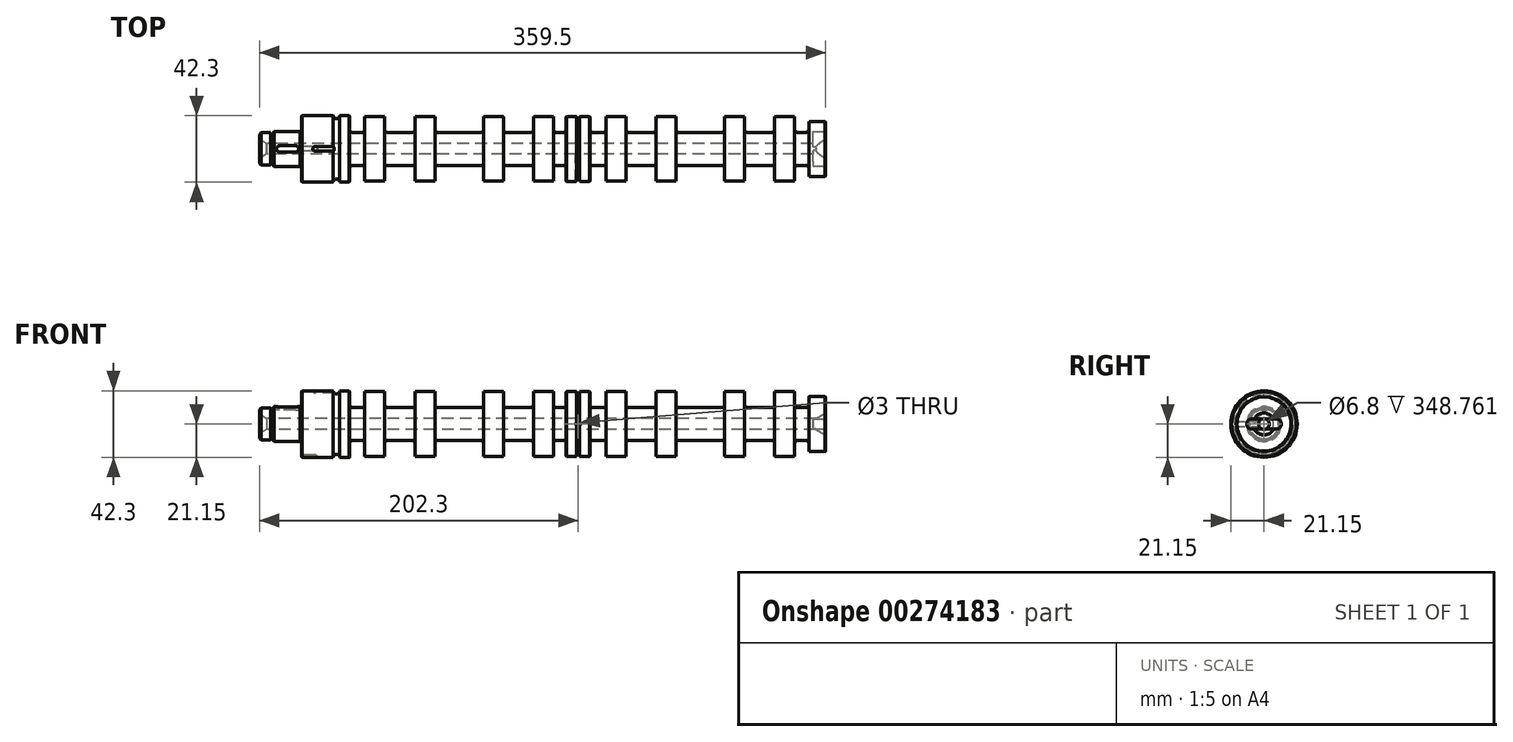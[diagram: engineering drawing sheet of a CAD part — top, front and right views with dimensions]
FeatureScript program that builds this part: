
annotation { "Feature Type Name" : "Feature", "Feature Type Description" : "" }
export const myFeature = defineFeature(function(context is Context, id is Id, definition is map)
    precondition{}
    {
        {
            var Q0;
            Q0=qCreatedBy(makeId("Front.planeOp"),FACE);
            var sketch = newSketch(context, id + "F0", { "sketchPlane" : qUnion([Q0])});
            skLineSegment(sketch, "E0", {"start": v(0, 0) * mm, "end": v(0, 10.23) * mm});
            skLineSegment(sketch, "E1", {"start": v(0, 10.23) * mm, "end": v(7.5, 10.23) * mm});
            skLineSegment(sketch, "E2", {"start": v(7.5, 10.23) * mm, "end": v(7.5, 9.4) * mm});
            skLineSegment(sketch, "E3", {"start": v(7.5, 9.4) * mm, "end": v(9, 9.4) * mm});
            skLineSegment(sketch, "E4", {"start": v(9, 9.4) * mm, "end": v(9, 11.1) * mm});
            skLineSegment(sketch, "E5", {"start": v(9, 11.1) * mm, "end": v(25.8, 11.1) * mm});
            skLineSegment(sketch, "E6", {"start": v(26.8, 11.1) * mm, "end": v(26.8, 21.15) * mm});
            skLineSegment(sketch, "E7", {"start": v(57.3, 21.15) * mm, "end": v(57.3, 10.5) * mm});
            skLineSegment(sketch, "E8", {"start": v(57.3, 10.5) * mm, "end": v(66.8, 10.5) * mm});
            skLineSegment(sketch, "E9", {"start": v(66.8, 10.5) * mm, "end": v(66.8, 20.55) * mm});
            skLineSegment(sketch, "E10", {"start": v(79.5, 20.55) * mm, "end": v(79.5, 10.5) * mm});
            skLineSegment(sketch, "E11", {"start": v(79.5, 10.5) * mm, "end": v(98.7, 10.5) * mm});
            skLineSegment(sketch, "E12", {"start": v(98.7, 10.5) * mm, "end": v(98.7, 20.55) * mm});
            skLineSegment(sketch, "E13", {"start": v(25.8, 11.1) * mm, "end": v(25.8, 10.6) * mm});
            skLineSegment(sketch, "E14", {"start": v(25.8, 10.6) * mm, "end": v(26.8, 10.6) * mm});
            skLineSegment(sketch, "E15", {"start": v(26.8, 10.6) * mm, "end": v(26.8, 11.1) * mm});
            skLineSegment(sketch, "E16.trimOffspring", {"start": v(50.8, 21.15) * mm, "end": v(57.3, 21.15) * mm});
            skLineSegment(sketch, "E17", {"start": v(111.4, 20.55) * mm, "end": v(111.4, 10.5) * mm});
            skLineSegment(sketch, "E18", {"start": v(111.4, 10.5) * mm, "end": v(142.2, 10.5) * mm});
            skLineSegment(sketch, "E19", {"start": v(142.2, 10.5) * mm, "end": v(142.2, 20.55) * mm});
            skLineSegment(sketch, "E20", {"start": v(154.9, 20.55) * mm, "end": v(154.9, 10.5) * mm});
            skLineSegment(sketch, "E21", {"start": v(154.9, 10.5) * mm, "end": v(173.9, 10.5) * mm});
            skLineSegment(sketch, "E22", {"start": v(173.9, 10.5) * mm, "end": v(173.9, 20.55) * mm});
            skLineSegment(sketch, "E23", {"start": v(186.6, 20.55) * mm, "end": v(186.6, 10.5) * mm});
            skLineSegment(sketch, "E24", {"start": v(186.6, 10.5) * mm, "end": v(194.8, 10.5) * mm});
            skLineSegment(sketch, "E25", {"start": v(194.8, 10.5) * mm, "end": v(194.8, 20.6) * mm});
            skLineSegment(sketch, "E26", {"start": v(194.8, 20.6) * mm, "end": v(201.3, 20.6) * mm});
            skLineSegment(sketch, "E27", {"start": v(203.3, 20.61) * mm, "end": v(209.8, 20.61) * mm});
            skLineSegment(sketch, "E28", {"start": v(209.8, 20.6) * mm, "end": v(209.8, 10.5) * mm});
            skArc(sketch, "E29", {"start": v(201.3, 20.6) * mm, "mid": v(202.3, 19.6) * mm, "end": v(203.3, 20.6) * mm});
            skLineSegment(sketch, "E30", {"start": v(0, 0) * mm, "end": v(359.5, 0) * mm});
            skLineSegment(sketch, "E31", {"start": v(186.6, 20.55) * mm, "end": v(173.9, 20.55) * mm});
            skLineSegment(sketch, "E32.trimOffspring", {"start": v(154.9, 20.55) * mm, "end": v(142.2, 20.55) * mm});
            skLineSegment(sketch, "E33.trimOffspring", {"start": v(111.4, 20.55) * mm, "end": v(98.7, 20.55) * mm});
            skLineSegment(sketch, "E34.trimOffspring", {"start": v(79.5, 20.55) * mm, "end": v(66.8, 20.55) * mm});
            skLineSegment(sketch, "E35", {"start": v(220.1, 10.5) * mm, "end": v(220.1, 20.55) * mm});
            skLineSegment(sketch, "E36", {"start": v(232.8, 20.55) * mm, "end": v(232.8, 10.5) * mm});
            skLineSegment(sketch, "E37", {"start": v(251.8, 10.5) * mm, "end": v(251.8, 20.55) * mm});
            skLineSegment(sketch, "E38", {"start": v(264.5, 20.55) * mm, "end": v(264.5, 10.5) * mm});
            skLineSegment(sketch, "E39", {"start": v(295.4, 10.5) * mm, "end": v(295.4, 20.55) * mm});
            skLineSegment(sketch, "E40", {"start": v(308.1, 20.55) * mm, "end": v(308.1, 10.5) * mm});
            skLineSegment(sketch, "E41", {"start": v(327.2, 10.5) * mm, "end": v(327.2, 20.55) * mm});
            skLineSegment(sketch, "E42", {"start": v(339.9, 20.55) * mm, "end": v(339.9, 10.5) * mm});
            skLineSegment(sketch, "E43", {"start": v(339.9, 20.55) * mm, "end": v(327.2, 20.55) * mm});
            skLineSegment(sketch, "E44.trimOffspring", {"start": v(308.1, 20.55) * mm, "end": v(295.4, 20.55) * mm});
            skLineSegment(sketch, "E45.trimOffspring", {"start": v(264.5, 20.55) * mm, "end": v(251.8, 20.55) * mm});
            skLineSegment(sketch, "E46.trimOffspring", {"start": v(232.8, 20.55) * mm, "end": v(220.1, 20.55) * mm});
            skLineSegment(sketch, "E47", {"start": v(348.8, 10.5) * mm, "end": v(348.8, 17.44) * mm});
            skLineSegment(sketch, "E48", {"start": v(348.8, 17.44) * mm, "end": v(359.5, 17.44) * mm});
            skLineSegment(sketch, "E49", {"start": v(359.5, 17.44) * mm, "end": v(359.5, 0) * mm});
            skLineSegment(sketch, "E50", {"start": v(46.8, 21.15) * mm, "end": v(26.8, 21.15) * mm});
            skArc(sketch, "E51", {"start": v(46.8, 21.15) * mm, "mid": v(48.8, 19.15) * mm, "end": v(50.8, 21.15) * mm});
            skLineSegment(sketch, "E52", {"start": v(209.8, 10.5) * mm, "end": v(220.1, 10.5) * mm});
            skLineSegment(sketch, "E53.trimOffspring", {"start": v(232.8, 10.5) * mm, "end": v(251.8, 10.5) * mm});
            skLineSegment(sketch, "E54.trimOffspring", {"start": v(264.5, 10.5) * mm, "end": v(295.4, 10.5) * mm});
            skLineSegment(sketch, "E55.trimOffspring", {"start": v(308.1, 10.5) * mm, "end": v(327.2, 10.5) * mm});
            skLineSegment(sketch, "E56.trimOffspring", {"start": v(339.9, 10.5) * mm, "end": v(348.8, 10.5) * mm});
            skSolve(sketch);
        }
        {
            var Q0;
            Q0 = qSketchRegion(id + "F0", true);
            var Q1;
            Q1=sQuery(id+"F0.wireOp",EDGE,"E30");
            revolve(context, id + "F1", {"entities" : qUnion([Q0]), "axis" : qUnion([Q1]), "revolveType" : RevolveType.FULL});
        }
        {
            var Q0;
            Q0=makeQuery(id+"F1.opRevolve","SWEPT_EDGE",EDGE,{"disambiguationData":[OSD([sQuery(id+"F0.wireOp",EDGE,"E42"),sQuery(id+"F0.wireOp",EDGE,"E56.trimOffspring")])]});
            var Q1;
            Q1=makeQuery(id+"F1.opRevolve","SWEPT_EDGE",EDGE,{"disambiguationData":[OSD([sQuery(id+"F0.wireOp",EDGE,"E40"),sQuery(id+"F0.wireOp",EDGE,"E55.trimOffspring")])]});
            var Q2;
            Q2=makeQuery(id+"F1.opRevolve","SWEPT_EDGE",EDGE,{"disambiguationData":[OSD([sQuery(id+"F0.wireOp",EDGE,"E38"),sQuery(id+"F0.wireOp",EDGE,"E54.trimOffspring")])]});
            var Q3;
            Q3=makeQuery(id+"F1.opRevolve","SWEPT_EDGE",EDGE,{"disambiguationData":[OSD([sQuery(id+"F0.wireOp",EDGE,"E36"),sQuery(id+"F0.wireOp",EDGE,"E53.trimOffspring")])]});
            var Q4;
            Q4=makeQuery(id+"F1.opRevolve","SWEPT_EDGE",EDGE,{"disambiguationData":[OSD([sQuery(id+"F0.wireOp",EDGE,"E28"),sQuery(id+"F0.wireOp",EDGE,"E52")])]});
            var Q5;
            Q5=makeQuery(id+"F1.opRevolve","SWEPT_EDGE",EDGE,{"disambiguationData":[OSD([sQuery(id+"F0.wireOp",EDGE,"E23"),sQuery(id+"F0.wireOp",EDGE,"E24")])]});
            var Q6;
            Q6=makeQuery(id+"F1.opRevolve","SWEPT_EDGE",EDGE,{"disambiguationData":[OSD([sQuery(id+"F0.wireOp",EDGE,"E20"),sQuery(id+"F0.wireOp",EDGE,"E21")])]});
            var Q7;
            Q7=makeQuery(id+"F1.opRevolve","SWEPT_EDGE",EDGE,{"disambiguationData":[OSD([sQuery(id+"F0.wireOp",EDGE,"E17"),sQuery(id+"F0.wireOp",EDGE,"E18")])]});
            var Q8;
            Q8=makeQuery(id+"F1.opRevolve","SWEPT_EDGE",EDGE,{"disambiguationData":[OSD([sQuery(id+"F0.wireOp",EDGE,"E10"),sQuery(id+"F0.wireOp",EDGE,"E11")])]});
            var Q9;
            Q9=makeQuery(id+"F1.opRevolve","SWEPT_EDGE",EDGE,{"disambiguationData":[OSD([sQuery(id+"F0.wireOp",EDGE,"E7"),sQuery(id+"F0.wireOp",EDGE,"E8")])]});
            var Q10;
            Q10=makeQuery(id+"F1.opRevolve","SWEPT_EDGE",EDGE,{"disambiguationData":[OSD([sQuery(id+"F0.wireOp",EDGE,"E47"),sQuery(id+"F0.wireOp",EDGE,"E56.trimOffspring")])]});
            var Q11;
            Q11=makeQuery(id+"F1.opRevolve","SWEPT_EDGE",EDGE,{"disambiguationData":[OSD([sQuery(id+"F0.wireOp",EDGE,"E41"),sQuery(id+"F0.wireOp",EDGE,"E55.trimOffspring")])]});
            var Q12;
            Q12=makeQuery(id+"F1.opRevolve","SWEPT_EDGE",EDGE,{"disambiguationData":[OSD([sQuery(id+"F0.wireOp",EDGE,"E39"),sQuery(id+"F0.wireOp",EDGE,"E54.trimOffspring")])]});
            var Q13;
            Q13=makeQuery(id+"F1.opRevolve","SWEPT_EDGE",EDGE,{"disambiguationData":[OSD([sQuery(id+"F0.wireOp",EDGE,"E37"),sQuery(id+"F0.wireOp",EDGE,"E53.trimOffspring")])]});
            var Q14;
            Q14=makeQuery(id+"F1.opRevolve","SWEPT_EDGE",EDGE,{"disambiguationData":[OSD([sQuery(id+"F0.wireOp",EDGE,"E35"),sQuery(id+"F0.wireOp",EDGE,"E52")])]});
            var Q15;
            Q15=makeQuery(id+"F1.opRevolve","SWEPT_EDGE",EDGE,{"disambiguationData":[OSD([sQuery(id+"F0.wireOp",EDGE,"E21"),sQuery(id+"F0.wireOp",EDGE,"E22")])]});
            var Q16;
            Q16=makeQuery(id+"F1.opRevolve","SWEPT_EDGE",EDGE,{"disambiguationData":[OSD([sQuery(id+"F0.wireOp",EDGE,"E18"),sQuery(id+"F0.wireOp",EDGE,"E19")])]});
            var Q17;
            Q17=makeQuery(id+"F1.opRevolve","SWEPT_EDGE",EDGE,{"disambiguationData":[OSD([sQuery(id+"F0.wireOp",EDGE,"E11"),sQuery(id+"F0.wireOp",EDGE,"E12")])]});
            var Q18;
            Q18=makeQuery(id+"F1.opRevolve","SWEPT_EDGE",EDGE,{"disambiguationData":[OSD([sQuery(id+"F0.wireOp",EDGE,"E8"),sQuery(id+"F0.wireOp",EDGE,"E9")])]});
            var Q19;
            Q19=makeQuery(id+"F1.opRevolve","SWEPT_EDGE",EDGE,{"disambiguationData":[OSD([sQuery(id+"F0.wireOp",EDGE,"E24"),sQuery(id+"F0.wireOp",EDGE,"E25")])]});
            fillet(context, id + "F2", {"entities" : qUnion([Q0, Q1, Q2, Q3, Q4, Q5, Q6, Q7, Q8, Q9, Q10, Q11, Q12, Q13, Q14, Q15, Q16, Q17, Q18, Q19]), "radius" : 1.6 * mm, "tangentPropagation" : true, "allowEdgeOverflow" : false});
        }
        {
            var Q0;
            Q0=makeQuery(id+"F1.opRevolve","SWEPT_EDGE",EDGE,{"disambiguationData":[OSD([sQuery(id+"F0.wireOp",EDGE,"E0"),sQuery(id+"F0.wireOp",EDGE,"E1")])]});
            chamfer(context, id + "F3", {"entities" : qUnion([Q0]), "width" : 1 * mm, "tangentPropagation" : true});
        }
        {
            var Q0;
            Q0=makeQuery(id+"F1.opRevolve","SWEPT_EDGE",EDGE,{"disambiguationData":[OSD([sQuery(id+"F0.wireOp",EDGE,"E7"),sQuery(id+"F0.wireOp",EDGE,"E16.trimOffspring")])]});
            var Q1;
            Q1=makeQuery(id+"F1.opRevolve","SWEPT_EDGE",EDGE,{"disambiguationData":[OSD([sQuery(id+"F0.wireOp",EDGE,"E25"),sQuery(id+"F0.wireOp",EDGE,"E26")])]});
            var Q2;
            Q2=makeQuery(id+"F1.opRevolve","SWEPT_EDGE",EDGE,{"disambiguationData":[OSD([sQuery(id+"F0.wireOp",EDGE,"E27"),sQuery(id+"F0.wireOp",EDGE,"E28")])]});
            var Q3;
            Q3=makeQuery(id+"F1.opRevolve","SWEPT_EDGE",EDGE,{"disambiguationData":[OSD([sQuery(id+"F0.wireOp",EDGE,"E47"),sQuery(id+"F0.wireOp",EDGE,"E48")])]});
            var Q4;
            Q4=makeQuery(id+"F1.opRevolve","SWEPT_EDGE",EDGE,{"disambiguationData":[OSD([sQuery(id+"F0.wireOp",EDGE,"E48"),sQuery(id+"F0.wireOp",EDGE,"E49")])]});
            var Q5;
            Q5=makeQuery(id+"F1.opRevolve","SWEPT_EDGE",EDGE,{"disambiguationData":[OSD([sQuery(id+"F0.wireOp",EDGE,"E4"),sQuery(id+"F0.wireOp",EDGE,"E5")])]});
            var Q6;
            Q6=makeQuery(id+"F1.opRevolve","SWEPT_EDGE",EDGE,{"disambiguationData":[OSD([sQuery(id+"F0.wireOp",EDGE,"E6"),sQuery(id+"F0.wireOp",EDGE,"E50")])]});
            chamfer(context, id + "F4", {"entities" : qUnion([Q0, Q1, Q2, Q3, Q4, Q5, Q6]), "width" : 0.3 * mm, "tangentPropagation" : true});
        }
        {
            var Q0;
            Q0=makeQuery(id+"F1.opRevolve","SWEPT_EDGE",EDGE,{"disambiguationData":[OSD([sQuery(id+"F0.wireOp",EDGE,"E1"),sQuery(id+"F0.wireOp",EDGE,"E2")])]});
            chamfer(context, id + "F5", {"entities" : qUnion([Q0]), "chamferType" : ChamferType.OFFSET_ANGLE, "width" : 0.5 * mm, "oppositeDirection" : false, "angle" : 60 * degree, "tangentPropagation" : true});
        }
        {
            var Q0;
            Q0=makeQuery(id+"F1.opRevolve","SWEPT_EDGE",EDGE,{"disambiguationData":[OSD([sQuery(id+"F0.wireOp",EDGE,"E14"),sQuery(id+"F0.wireOp",EDGE,"E15")])]});
            var Q1;
            Q1=makeQuery(id+"F1.opRevolve","SWEPT_EDGE",EDGE,{"disambiguationData":[OSD([sQuery(id+"F0.wireOp",EDGE,"E13"),sQuery(id+"F0.wireOp",EDGE,"E14")])]});
            var Q2;
            Q2=makeQuery(id+"F1.opRevolve","SWEPT_EDGE",EDGE,{"disambiguationData":[OSD([sQuery(id+"F0.wireOp",EDGE,"E3"),sQuery(id+"F0.wireOp",EDGE,"E4")])]});
            var Q3;
            Q3=makeQuery(id+"F1.opRevolve","SWEPT_EDGE",EDGE,{"disambiguationData":[OSD([sQuery(id+"F0.wireOp",EDGE,"E2"),sQuery(id+"F0.wireOp",EDGE,"E3")])]});
            var Q4;
            Q4=makeQuery(id+"F5.opChamfer","BLEND_EDGE",EDGE,{"blendedFrom":[makeQuery(id+"F1.opRevolve","SWEPT_EDGE",EDGE,{"disambiguationData":[OSD([sQuery(id+"F0.wireOp",EDGE,"E1"),sQuery(id+"F0.wireOp",EDGE,"E2")])]}),makeQuery(id+"F1.opRevolve","SWEPT_FACE",FACE,{"disambiguationData":[OSD([sQuery(id+"F0.wireOp",EDGE,"E3")])]})],"blendedInto":[makeQuery(id+"F1.opRevolve","SWEPT_FACE",FACE,{"disambiguationData":[OSD([sQuery(id+"F0.wireOp",EDGE,"E3")])]})]});
            fillet(context, id + "F6", {"entities" : qUnion([Q0, Q1, Q2, Q3, Q4]), "radius" : 0.5 * mm, "tangentPropagation" : true, "allowEdgeOverflow" : false});
        }
        {
            var Q0;
            Q0=makeQuery(id+"F1.opRevolve","SWEPT_FACE",FACE,{"disambiguationData":[OSD([sQuery(id+"F0.wireOp",EDGE,"E49")])]});
            var sketch = newSketch(context, id + "F7", { "sketchPlane" : qUnion([Q0])});
            skLineSegment(sketch, "E57", {"start": v(-8, 3.17) * mm, "end": v(8, 3.17) * mm});
            skLineSegment(sketch, "E58", {"start": v(11, 0.18) * mm, "end": v(11, -0.17) * mm});
            skLineSegment(sketch, "E59", {"start": v(8, -3.17) * mm, "end": v(-8, -3.18) * mm});
            skLineSegment(sketch, "E60", {"start": v(-11, -0.18) * mm, "end": v(-11, 0.17) * mm});
            skPoint(sketch, "E61.visualSharp", {"position": v(-11, 3.17) * mm});
            skArc(sketch, "E61.filletArc", {"start": v(-8, 3.17) * mm, "mid": v(-10.12, 2.3) * mm, "end": v(-11, 0.17) * mm});
            skPoint(sketch, "E62.visualSharp", {"position": v(-11, -3.18) * mm});
            skArc(sketch, "E62.filletArc", {"start": v(-11, -0.18) * mm, "mid": v(-10.12, -2.3) * mm, "end": v(-8, -3.18) * mm});
            skPoint(sketch, "E63.visualSharp", {"position": v(11, 3.17) * mm});
            skArc(sketch, "E63.filletArc", {"start": v(11, 0.18) * mm, "mid": v(10.12, 2.3) * mm, "end": v(8, 3.17) * mm});
            skPoint(sketch, "E64.visualSharp", {"position": v(11, -3.17) * mm});
            skArc(sketch, "E64.filletArc", {"start": v(8, -3.17) * mm, "mid": v(10.12, -2.3) * mm, "end": v(11, -0.17) * mm});
            skSolve(sketch);
        }
        {
            var Q0;
            {var subQ1=sQuery(id+"F7.wireOp",EDGE,"E61.filletArc");Q0=makeQuery(id+"F7.imprint","IMPRINT",FACE,{"disambiguationData":[TD([[makeQuery(id+"F7.imprint","IMPRINT",EDGE,{"derivedFrom":subQ1}),1.0]])]});}
            var Q1;
            {var subQ1=sQuery(id+"F7.wireOp",EDGE,"E63.filletArc");Q1=makeQuery(id+"F7.imprint","IMPRINT",FACE,{"disambiguationData":[TD([[makeQuery(id+"F7.imprint","IMPRINT",EDGE,{"derivedFrom":subQ1}),1.0]])]});}
            var Q2;
            {var subQ0=sQuery(id+"F7.wireOp",EDGE,"E57");var subQ1=makeQuery(id+"F1.opRevolve","SWEPT_FACE",FACE,{"disambiguationData":[OSD([sQuery(id+"F0.wireOp",EDGE,"E49")])]});var subQ2=makeQuery(id+"FjbEp7hMja5GWEH_1.opChamfer","BLEND_EDGE",EDGE,{"blendedFrom":[makeQuery(id+"FVFhnxNaDeFgwCE_1.boolean.opBoolean","INTERSECT",EDGE,{"derivedFrom":[subQ1,makeQuery(id+"FVFhnxNaDeFgwCE_1.opExtrude","SWEPT_FACE",FACE,{"disambiguationData":[OSD([sQuery(id+"FgBfjt2P3U3ezcS_1.wireOp",EDGE,"Z8qlCyaP-uUiq-p7OV-OB7W-ui8Vbjvxlwgm")])]})]}),subQ1],"blendedInto":[subQ1]});var subQ3=makeQuery(id+"F7.imprint","INTERSECT",VERTEX,{"disambiguationData":[OD(0.0)],"derivedFrom":[subQ2,subQ0]});Q2=makeQuery(id+"F7.imprint","IMPRINT",FACE,{"disambiguationData":[TD([[makeQuery(id+"F7.imprint","IMPRINT",EDGE,{"disambiguationData":[TD([[subQ3,-1.0]])],"derivedFrom":subQ0}),-1.0]])]});}
            extrude(context, id + "F8", {"entities" : qUnion([Q0, Q1, Q2]), "operationType" : NewBodyOperationType.REMOVE, "oppositeDirection" : true, "depth" : 8 * mm});
        }
        {
            var Q0;
            Q0=qCreatedBy(makeId("Front.planeOp"),FACE);
            var sketch = newSketch(context, id + "F9", { "sketchPlane" : qUnion([Q0])});
            skLineSegment(sketch, "E65", {"start": v(33.8, 21.15) * mm, "end": v(33.8, 21.15) * mm});
            skLineSegment(sketch, "E66", {"start": v(35.3, 19.65) * mm, "end": v(48.8, 19.65) * mm});
            skLineSegment(sketch, "E67", {"start": v(48.8, 21.15) * mm, "end": v(48.8, 19.65) * mm});
            skPoint(sketch, "E68.visualSharp", {"position": v(33.8, 19.65) * mm});
            skArc(sketch, "E68.filletArc", {"start": v(33.8, 21.15) * mm, "mid": v(34.24, 20.09) * mm, "end": v(35.3, 19.65) * mm});
            skPoint(sketch, "E69.visualSharp", {"position": v(33.8, 22.64) * mm});
            skLineSegment(sketch, "E70", {"start": v(48.8, 21.15) * mm, "end": v(33.8, 21.15) * mm});
            skPoint(sketch, "E71.orphan", {"position": v(48.8, 22.65) * mm});
            skSolve(sketch);
        }
        {
            var Q0;
            Q0=makeQuery(id+"F9.imprint","IMPRINT",FACE,{"disambiguationData":[TD([[makeQuery(id+"F9.imprint","IMPRINT",EDGE,{"derivedFrom":sQuery(id+"F9.wireOp",EDGE,"E66")}),1.0]])]});
            var Q1;
            Q1=sQuery(id+"F9.wireOp",EDGE,"E70");
            revolve(context, id + "F10", {"operationType" : NewBodyOperationType.REMOVE, "entities" : qUnion([Q0]), "axis" : qUnion([Q1]), "revolveType" : RevolveType.FULL, "oppositeDirection" : true});
        }
        {
            var Q0;
            Q0=qCreatedBy(makeId("Front.planeOp"),FACE);
            var sketch = newSketch(context, id + "F11", { "sketchPlane" : qUnion([Q0])});
            skLineSegment(sketch, "E72", {"start": v(26.8, -19.65) * mm, "end": v(35.3, -19.65) * mm});
            skLineSegment(sketch, "E73", {"start": v(36.8, -21.15) * mm, "end": v(36.8, -21.15) * mm});
            skLineSegment(sketch, "E74", {"start": v(26.8, -21.15) * mm, "end": v(26.8, -19.65) * mm});
            skLineSegment(sketch, "E75", {"start": v(36.8, -21.15) * mm, "end": v(26.8, -21.15) * mm});
            skPoint(sketch, "E76.visualSharp", {"position": v(36.8, -19.65) * mm});
            skArc(sketch, "E76.filletArc", {"start": v(36.8, -21.15) * mm, "mid": v(36.36, -20.09) * mm, "end": v(35.3, -19.65) * mm});
            skSolve(sketch);
        }
        {
            var Q0;
            Q0 = qSketchRegion(id + "F11", true);
            var Q1;
            Q1=sQuery(id+"F11.wireOp",EDGE,"E75");
            revolve(context, id + "F12", {"operationType" : NewBodyOperationType.REMOVE, "entities" : qUnion([Q0]), "axis" : qUnion([Q1]), "revolveType" : RevolveType.FULL, "oppositeDirection" : true});
        }
        {
            var Q0;
            Q0=qCreatedBy(makeId("Front.planeOp"),FACE);
            var sketch = newSketch(context, id + "F13", { "sketchPlane" : qUnion([Q0])});
            skCircle(sketch, "E77", {"center": v(202.3, 0) * mm, "radius": 1.5 * mm});
            skSolve(sketch);
        }
        {
            var Q0;
            Q0 = qSketchRegion(id + "F13", true);
            extrude(context, id + "F14", {"entities" : qUnion([Q0]), "operationType" : NewBodyOperationType.REMOVE, "depth" : 45 * mm});
        }
        {
            var Q0;
            Q0=qCreatedBy(makeId("Front.planeOp"),FACE);
            var sketch = newSketch(context, id + "F15", { "sketchPlane" : qUnion([Q0])});
            skLineSegment(sketch, "E78", {"start": v(10.8, 11.1) * mm, "end": v(24.8, 11.1) * mm});
            skLineSegment(sketch, "E79", {"start": v(24.8, 11.1) * mm, "end": v(24.8, 8.9) * mm});
            skLineSegment(sketch, "E80", {"start": v(24.8, 8.9) * mm, "end": v(10.8, 8.9) * mm});
            skLineSegment(sketch, "E81", {"start": v(10.8, 8.9) * mm, "end": v(10.8, 11.1) * mm});
            skSolve(sketch);
        }
        {
            var Q0;
            Q0=makeQuery(id+"F15.imprint","IMPRINT",FACE,{"disambiguationData":[TD([[makeQuery(id+"F15.imprint","IMPRINT",EDGE,{"derivedFrom":sQuery(id+"F15.wireOp",EDGE,"E78")}),-1.0]])]});
            extrude(context, id + "F16", {"entities" : qUnion([Q0]), "operationType" : NewBodyOperationType.REMOVE, "endBound" : BoundingType.SYMMETRIC, "depth" : 4 * mm});
        }
        {
            var Q0;
            Q0=makeQuery(id+"F16.boolean.opBoolean","COPY",EDGE,{"derivedFrom":makeQuery(id+"F16.opExtrude","CAP_EDGE",EDGE,{"disambiguationData":[OSD([sQuery(id+"F15.wireOp",EDGE,"E79")])],"isStart":true})});
            var Q1;
            Q1=makeQuery(id+"F16.boolean.opBoolean","COPY",EDGE,{"derivedFrom":makeQuery(id+"F16.opExtrude","CAP_EDGE",EDGE,{"disambiguationData":[OSD([sQuery(id+"F15.wireOp",EDGE,"E79")])],"isStart":false})});
            var Q2;
            Q2=makeQuery(id+"F16.boolean.opBoolean","COPY",EDGE,{"derivedFrom":makeQuery(id+"F16.opExtrude","CAP_EDGE",EDGE,{"disambiguationData":[OSD([sQuery(id+"F15.wireOp",EDGE,"E81")])],"isStart":true})});
            var Q3;
            Q3=makeQuery(id+"F16.boolean.opBoolean","COPY",EDGE,{"derivedFrom":makeQuery(id+"F16.opExtrude","CAP_EDGE",EDGE,{"disambiguationData":[OSD([sQuery(id+"F15.wireOp",EDGE,"E81")])],"isStart":false})});
            fillet(context, id + "F17", {"entities" : qUnion([Q0, Q1, Q2, Q3]), "radius" : 2 * mm, "tangentPropagation" : true, "allowEdgeOverflow" : false});
        }
        {
            var Q0;
            Q0=makeQuery(id+"F1.opRevolve","SWEPT_FACE",FACE,{"disambiguationData":[OSD([sQuery(id+"F0.wireOp",EDGE,"E0")])]});
            var sketch = newSketch(context, id + "F18", { "sketchPlane" : qUnion([Q0])});
            skPoint(sketch, "E82", {"position": v(0, 0) * mm});
            skSolve(sketch);
        }
        {
            var Q0;
            Q0=sQuery(id+"F18.wireOp",VERTEX,"E82");
            var Q1;
            Q1=makeQuery(id+"F1.opRevolve","SWEPT_BODY",BODY,{"disambiguationData":[OSD([sQuery(id+"F0.wireOp",EDGE,"E0"),sQuery(id+"F0.wireOp",EDGE,"E1"),sQuery(id+"F0.wireOp",EDGE,"E2"),sQuery(id+"F0.wireOp",EDGE,"E3"),sQuery(id+"F0.wireOp",EDGE,"E4"),sQuery(id+"F0.wireOp",EDGE,"E5"),sQuery(id+"F0.wireOp",EDGE,"E6"),sQuery(id+"F0.wireOp",EDGE,"E7"),sQuery(id+"F0.wireOp",EDGE,"E8"),sQuery(id+"F0.wireOp",EDGE,"E9"),sQuery(id+"F0.wireOp",EDGE,"E10"),sQuery(id+"F0.wireOp",EDGE,"E11"),sQuery(id+"F0.wireOp",EDGE,"E12"),sQuery(id+"F0.wireOp",EDGE,"E13"),sQuery(id+"F0.wireOp",EDGE,"E14"),sQuery(id+"F0.wireOp",EDGE,"E15"),sQuery(id+"F0.wireOp",EDGE,"E16.trimOffspring"),sQuery(id+"F0.wireOp",EDGE,"E17"),sQuery(id+"F0.wireOp",EDGE,"E18"),sQuery(id+"F0.wireOp",EDGE,"E19"),sQuery(id+"F0.wireOp",EDGE,"E20"),sQuery(id+"F0.wireOp",EDGE,"E21"),sQuery(id+"F0.wireOp",EDGE,"E22"),sQuery(id+"F0.wireOp",EDGE,"E23"),sQuery(id+"F0.wireOp",EDGE,"E24"),sQuery(id+"F0.wireOp",EDGE,"E25"),sQuery(id+"F0.wireOp",EDGE,"E26"),sQuery(id+"F0.wireOp",EDGE,"E27"),sQuery(id+"F0.wireOp",EDGE,"E28"),sQuery(id+"F0.wireOp",EDGE,"E29"),sQuery(id+"F0.wireOp",EDGE,"E30"),sQuery(id+"F0.wireOp",EDGE,"E31"),sQuery(id+"F0.wireOp",EDGE,"E32.trimOffspring"),sQuery(id+"F0.wireOp",EDGE,"E33.trimOffspring"),sQuery(id+"F0.wireOp",EDGE,"E34.trimOffspring"),sQuery(id+"F0.wireOp",EDGE,"E35"),sQuery(id+"F0.wireOp",EDGE,"E36"),sQuery(id+"F0.wireOp",EDGE,"E37"),sQuery(id+"F0.wireOp",EDGE,"E38"),sQuery(id+"F0.wireOp",EDGE,"E39"),sQuery(id+"F0.wireOp",EDGE,"E40"),sQuery(id+"F0.wireOp",EDGE,"E41"),sQuery(id+"F0.wireOp",EDGE,"E42"),sQuery(id+"F0.wireOp",EDGE,"E43"),sQuery(id+"F0.wireOp",EDGE,"E44.trimOffspring"),sQuery(id+"F0.wireOp",EDGE,"E45.trimOffspring"),sQuery(id+"F0.wireOp",EDGE,"E46.trimOffspring"),sQuery(id+"F0.wireOp",EDGE,"E47"),sQuery(id+"F0.wireOp",EDGE,"E48"),sQuery(id+"F0.wireOp",EDGE,"E49"),sQuery(id+"F0.wireOp",EDGE,"E50"),sQuery(id+"F0.wireOp",EDGE,"E51"),sQuery(id+"F0.wireOp",EDGE,"E52"),sQuery(id+"F0.wireOp",EDGE,"E53.trimOffspring"),sQuery(id+"F0.wireOp",EDGE,"E54.trimOffspring"),sQuery(id+"F0.wireOp",EDGE,"E55.trimOffspring"),sQuery(id+"F0.wireOp",EDGE,"E56.trimOffspring")])]});
            hole(context, id + "F19", {"style" : HoleStyle.C_SINK, "endStyle" : HoleEndStyle.THROUGH, "holeDiameter" : 6.8 * mm, "cSinkDiameter" : 12 * mm, "cSinkAngle" : 60 * degree, "tappedDepth" : 26.25 * mm, "tapClearance" : 3, "startFromSketch" : true, "locations" : qUnion([Q0]), "scope" : qUnion([Q1])});
        }
        {
            var Q0;
            Q0=makeQuery(id+"F1.opRevolve","SWEPT_FACE",FACE,{"disambiguationData":[OSD([sQuery(id+"F0.wireOp",EDGE,"E49")])]});
            var sketch = newSketch(context, id + "F20", { "sketchPlane" : qUnion([Q0])});
            skPoint(sketch, "E83", {"position": v(0, 0) * mm});
            skSolve(sketch);
        }
        {
            var Q0;
            Q0=sQuery(id+"F20.wireOp",VERTEX,"E83");
            var Q1;
            Q1=makeQuery(id+"F1.opRevolve","SWEPT_BODY",BODY,{"disambiguationData":[OSD([sQuery(id+"F0.wireOp",EDGE,"E0"),sQuery(id+"F0.wireOp",EDGE,"E1"),sQuery(id+"F0.wireOp",EDGE,"E2"),sQuery(id+"F0.wireOp",EDGE,"E3"),sQuery(id+"F0.wireOp",EDGE,"E4"),sQuery(id+"F0.wireOp",EDGE,"E5"),sQuery(id+"F0.wireOp",EDGE,"E6"),sQuery(id+"F0.wireOp",EDGE,"E7"),sQuery(id+"F0.wireOp",EDGE,"E8"),sQuery(id+"F0.wireOp",EDGE,"E9"),sQuery(id+"F0.wireOp",EDGE,"E10"),sQuery(id+"F0.wireOp",EDGE,"E11"),sQuery(id+"F0.wireOp",EDGE,"E12"),sQuery(id+"F0.wireOp",EDGE,"E13"),sQuery(id+"F0.wireOp",EDGE,"E14"),sQuery(id+"F0.wireOp",EDGE,"E15"),sQuery(id+"F0.wireOp",EDGE,"E16.trimOffspring"),sQuery(id+"F0.wireOp",EDGE,"E17"),sQuery(id+"F0.wireOp",EDGE,"E18"),sQuery(id+"F0.wireOp",EDGE,"E19"),sQuery(id+"F0.wireOp",EDGE,"E20"),sQuery(id+"F0.wireOp",EDGE,"E21"),sQuery(id+"F0.wireOp",EDGE,"E22"),sQuery(id+"F0.wireOp",EDGE,"E23"),sQuery(id+"F0.wireOp",EDGE,"E24"),sQuery(id+"F0.wireOp",EDGE,"E25"),sQuery(id+"F0.wireOp",EDGE,"E26"),sQuery(id+"F0.wireOp",EDGE,"E27"),sQuery(id+"F0.wireOp",EDGE,"E28"),sQuery(id+"F0.wireOp",EDGE,"E29"),sQuery(id+"F0.wireOp",EDGE,"E30"),sQuery(id+"F0.wireOp",EDGE,"E31"),sQuery(id+"F0.wireOp",EDGE,"E32.trimOffspring"),sQuery(id+"F0.wireOp",EDGE,"E33.trimOffspring"),sQuery(id+"F0.wireOp",EDGE,"E34.trimOffspring"),sQuery(id+"F0.wireOp",EDGE,"E35"),sQuery(id+"F0.wireOp",EDGE,"E36"),sQuery(id+"F0.wireOp",EDGE,"E37"),sQuery(id+"F0.wireOp",EDGE,"E38"),sQuery(id+"F0.wireOp",EDGE,"E39"),sQuery(id+"F0.wireOp",EDGE,"E40"),sQuery(id+"F0.wireOp",EDGE,"E41"),sQuery(id+"F0.wireOp",EDGE,"E42"),sQuery(id+"F0.wireOp",EDGE,"E43"),sQuery(id+"F0.wireOp",EDGE,"E44.trimOffspring"),sQuery(id+"F0.wireOp",EDGE,"E45.trimOffspring"),sQuery(id+"F0.wireOp",EDGE,"E46.trimOffspring"),sQuery(id+"F0.wireOp",EDGE,"E47"),sQuery(id+"F0.wireOp",EDGE,"E48"),sQuery(id+"F0.wireOp",EDGE,"E49"),sQuery(id+"F0.wireOp",EDGE,"E50"),sQuery(id+"F0.wireOp",EDGE,"E51"),sQuery(id+"F0.wireOp",EDGE,"E52"),sQuery(id+"F0.wireOp",EDGE,"E53.trimOffspring"),sQuery(id+"F0.wireOp",EDGE,"E54.trimOffspring"),sQuery(id+"F0.wireOp",EDGE,"E55.trimOffspring"),sQuery(id+"F0.wireOp",EDGE,"E56.trimOffspring")])]});
            hole(context, id + "F21", {"style" : HoleStyle.C_SINK, "endStyle" : HoleEndStyle.BLIND, "holeDiameter" : 6.8 * mm, "cSinkDiameter" : 14 * mm, "cSinkAngle" : 60 * degree, "holeDepth" : 30 * mm, "tappedDepth" : 26.25 * mm, "tapClearance" : 3, "startFromSketch" : true, "locations" : qUnion([Q0]), "scope" : qUnion([Q1])});
        }
    });
